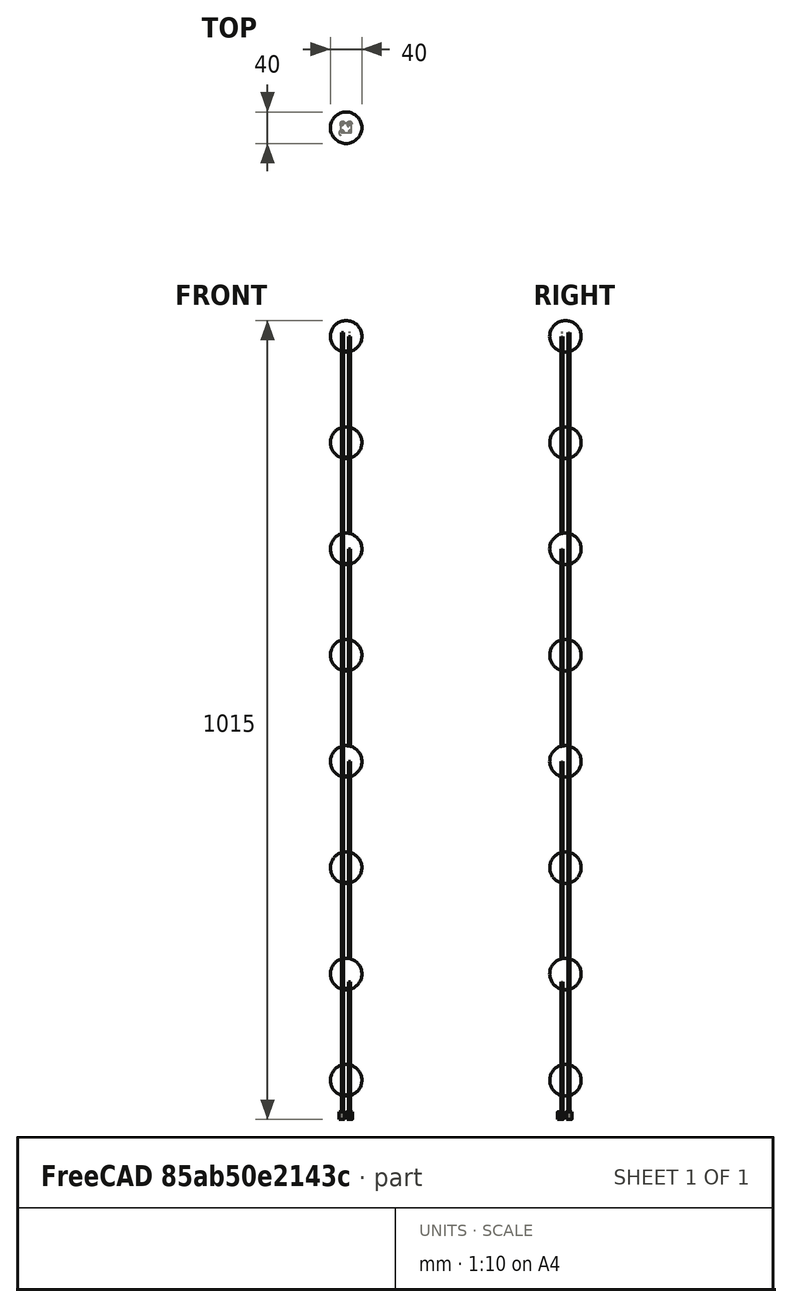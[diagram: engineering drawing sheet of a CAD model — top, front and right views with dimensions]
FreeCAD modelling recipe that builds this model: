
FCSTD DOCUMENT  (FreeCAD 0.16R)
Label: column
License: All rights reserved
LicenseURL: http://en.wikipedia.org/wiki/All_rights_reserved
objects: Part::Cylinder×12, Part::Compound×4, App::DocumentObjectGroup×3, Part::Feature×1, Part::Box×1, Part::Sphere×1, Part::FeaturePython×1
note: 20 computed .brp shape members not serialized (recipe doc carries the construction recipe); baked Part::Feature solids carry a one-line shape summary decoded from their .brp

FEATURE [Part::Cylinder] Cylinder  label="Power"
  Angle = 360
  Height = 1000
  Placement = pos=(-4.5,-4.5,0) rot=(0,0,1;0rad)
  Radius = 1.25
FEATURE [Part::Feature] Cylinder001  label="Ground"
  Placement = pos=(4.5,4.5,0) rot=(0,0,1;0rad)
  shape: bbox 2.5 x 2.5 x 1000 mm, 3 faces (baked)
FEATURE [Part::Cylinder] Cylinder002  label="Plug1"
  Angle = 360
  Height = 10
  Placement = pos=(-5.54596,-6.54595,0) rot=(0,0,1;0rad)
  Radius = 3.5
FEATURE [Part::Cylinder] Cylinder003  label="Plug002"
  Angle = 360
  Height = 10
  Placement = pos=(-4.5,4.5,0) rot=(0,0,1;0rad)
  Radius = 3.5
FEATURE [Part::Cylinder] Cylinder004  label="Plug003"
  Angle = 360
  Height = 10
  Placement = pos=(4.5,4.5,0) rot=(0,0,1;0rad)
  Radius = 3.5
FEATURE [Part::Cylinder] Cylinder005  label="Data In"
  Angle = 360
  Height = 50
  Placement = pos=(-4.5,4.5,0) rot=(0,0,1;0rad)
  Radius = 1.25
FEATURE [Part::Cylinder] Cylinder006  label="Data In001"
  Angle = 360
  Height = 175
  Placement = pos=(4.5,-4.5,0) rot=(0,0,1;0rad)
  Radius = 1.25
FEATURE [Part::Cylinder] Cylinder007  label="Data In002"
  Angle = 360
  Height = 155
  Placement = pos=(-4.5,4.5,165) rot=(0,0,1;0rad)
  Radius = 1.25
FEATURE [Part::Cylinder] Cylinder008  label="Data In003"
  Angle = 360
  Height = 155
  Placement = pos=(4.5,-4.5,300) rot=(0,0,1;0rad)
  Radius = 1.25
FEATURE [Part::Cylinder] Cylinder009  label="Data In004"
  Angle = 360
  Height = 155
  Placement = pos=(-4.5,4.5,435) rot=(0,0,1;0rad)
  Radius = 1.25
FEATURE [Part::Cylinder] Cylinder010  label="Data In005"
  Angle = 360
  Height = 155
  Placement = pos=(4.5,-4.5,570) rot=(0,0,1;0rad)
  Radius = 1.25
FEATURE [Part::Cylinder] Cylinder011  label="Data In006"
  Angle = 360
  Height = 155
  Placement = pos=(-4.5,4.5,705) rot=(0,0,1;0rad)
  Radius = 1.25
FEATURE [Part::Cylinder] Cylinder012  label="Data In007"
  Angle = 360
  Height = 155
  Placement = pos=(4.5,-4.5,840) rot=(0,0,1;0rad)
  Radius = 1.25
FEATURE [App::DocumentObjectGroup] Group  label="Data lines"
  Group = -> [Cylinder006,Cylinder007,Cylinder008,Cylinder009,Cylinder010,Cylinder011,Cylinder012]
FEATURE [App::DocumentObjectGroup] Group002  label="Balls"
FEATURE [Part::Box] Box  label="Cube"
  Height = 1.6
  Length = 13
  Placement = pos=(-6.5,-6.5,30) rot=(0,0,1;0rad)
  Width = 13
FEATURE [Part::Compound] Compound  label="Power Wire"
  Links = -> [Cylinder,Cylinder002]
FEATURE [Part::Compound] Compound001  label="Ground Wire"
  Links = -> [Cylinder001,Cylinder004]
FEATURE [Part::Compound] Compound002  label="Data line"
  Links = -> [Cylinder005,Cylinder003]
FEATURE [Part::Sphere] Sphere
  Angle1 = -90
  Angle2 = 90
  Angle3 = 360
  Placement = pos=(0,0,50) rot=(0,0,1;0rad)
  Radius = 20
FEATURE [Part::Compound] Compound003  label="Board1"
  Links = -> [Box,Sphere]
FEATURE [App::DocumentObjectGroup] Group001  label="Boards"
  Group = -> [Compound003]
FEATURE [Part::FeaturePython] Array  # Draft array (typed FeaturePython)
  Angle = 360
  ArrayType = 0
  Axis = (0,0,1)
  Base = -> Compound003
  Center = (0,0,0)
  Fuse = false
  IntervalAxis = (0,0,0)
  IntervalX = (1,0,0)
  IntervalY = (0,1,0)
  IntervalZ = (0,0,135)
  NumberPolar = 1
  NumberX = 1
  NumberY = 1
  NumberZ = 8
